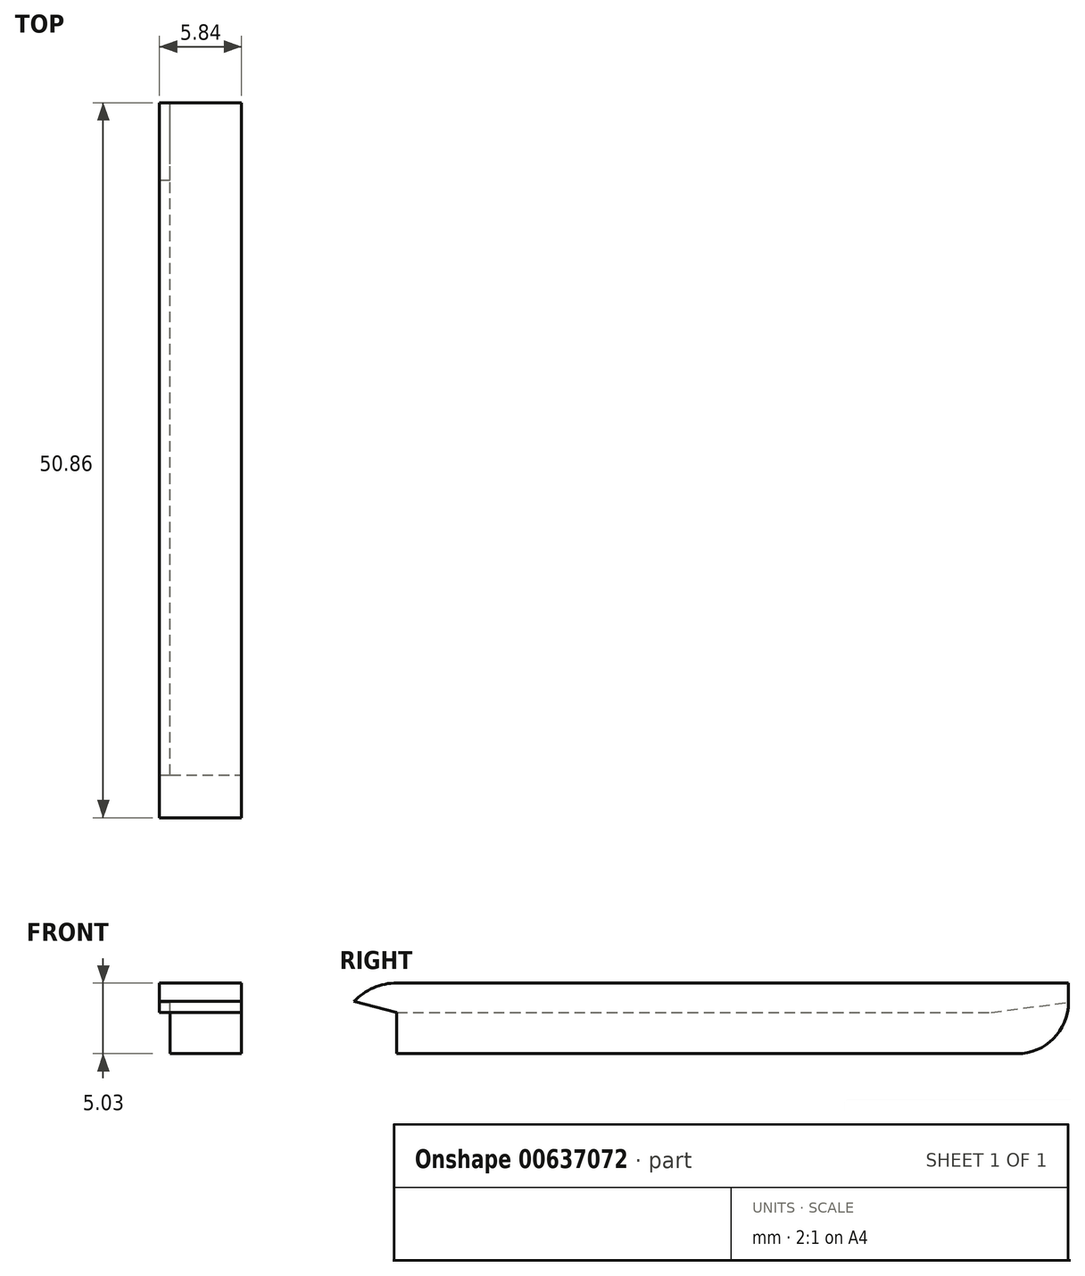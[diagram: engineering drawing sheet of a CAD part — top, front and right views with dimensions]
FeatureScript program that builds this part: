
annotation { "Feature Type Name" : "Feature", "Feature Type Description" : "" }
export const myFeature = defineFeature(function(context is Context, id is Id, definition is map)
    precondition{}
    {
        {
            var Q0;
            Q0=qCreatedBy(makeId("Right.planeOp"),FACE);
            var sketch = newSketch(context, id + "F0", { "sketchPlane" : qUnion([Q0])});
            skLineSegment(sketch, "E0", {"start": v(-27.86, 2.08) * mm, "end": v(14.45, 2.08) * mm});
            skArc(sketch, "E1", {"start": v(-27.86, 2.08) * mm, "mid": v(-29.52, 1.74) * mm, "end": v(-30.9, 0.77) * mm});
            skLineSegment(sketch, "E2", {"start": v(-30.9, 0.77) * mm, "end": v(-27.86, -0.01) * mm});
            skLineSegment(sketch, "E3", {"start": v(-27.86, 2.08) * mm, "end": v(-27.86, -2.95) * mm});
            skLineSegment(sketch, "E4", {"start": v(-27.86, -2.95) * mm, "end": v(14.45, -2.95) * mm});
            skArc(sketch, "E5", {"start": v(-27.86, -2.95) * mm, "mid": v(-30.18, -1.82) * mm, "end": v(-30.7, 0.71) * mm});
            skLineSegment(sketch, "E6", {"start": v(19.45, 2.08) * mm, "end": v(14.45, 2.08) * mm});
            skLineSegment(sketch, "E7", {"start": v(-27.86, -0.01) * mm, "end": v(14.45, -0.01) * mm});
            skLineSegment(sketch, "E8", {"start": v(14.45, -0.01) * mm, "end": v(14.45, 2.08) * mm});
            skLineSegment(sketch, "E9", {"start": v(14.45, -0.01) * mm, "end": v(14.45, -2.95) * mm});
            skArc(sketch, "E10", {"start": v(16.29, -2.95) * mm, "mid": v(18.88, -1.88) * mm, "end": v(19.95, 0.71) * mm});
            skLineSegment(sketch, "E11", {"start": v(16.29, -2.95) * mm, "end": v(14.45, -2.95) * mm});
            skLineSegment(sketch, "E12", {"start": v(14.45, -0.01) * mm, "end": v(19.95, 0.71) * mm});
            skLineSegment(sketch, "E13", {"start": v(19.95, 0.71) * mm, "end": v(19.95, 2.08) * mm});
            skLineSegment(sketch, "E14", {"start": v(19.95, 2.08) * mm, "end": v(19.45, 2.08) * mm});
            skSolve(sketch);
        }
        {
            var Q0;
            Q0=makeQuery(id+"F0.imprint","IMPRINT",FACE,{"disambiguationData":[TD([[makeQuery(id+"F0.imprint","IMPRINT",EDGE,{"derivedFrom":sQuery(id+"F0.wireOp",EDGE,"E6")}),1.0]])]});
            var Q1;
            {var subQ0=sQuery(id+"F0.wireOp",EDGE,"E0");Q1=makeQuery(id+"F0.imprint","IMPRINT",FACE,{"disambiguationData":[TD([[makeQuery(id+"F0.imprint","IMPRINT",EDGE,{"derivedFrom":subQ0}),-1.0]])]});}
            var Q2;
            {var subQ0=sQuery(id+"F0.wireOp",EDGE,"E1");Q2=makeQuery(id+"F0.imprint","IMPRINT",FACE,{"disambiguationData":[TD([[makeQuery(id+"F0.imprint","IMPRINT",EDGE,{"derivedFrom":subQ0}),1.0]])]});}
            extrude(context, id + "F1", {"entities" : qUnion([Q0, Q1, Q2]), "oppositeDirection" : true, "depth" : 5.84 * mm, "offsetDistance" : 25.4 * mm});
        }
        {
            var Q0;
            {var subQ3=sQuery(id+"F0.wireOp",EDGE,"E5");Q0=makeQuery(id+"F0.imprint","IMPRINT",FACE,{"disambiguationData":[TD([[makeQuery(id+"F0.imprint","IMPRINT",EDGE,{"derivedFrom":subQ3}),-1.0]])]});}
            var Q1;
            {var subQ2=sQuery(id+"F0.wireOp",EDGE,"E4");Q1=makeQuery(id+"F0.imprint","IMPRINT",FACE,{"disambiguationData":[TD([[makeQuery(id+"F0.imprint","IMPRINT",EDGE,{"derivedFrom":subQ2}),1.0]])]});}
            var Q2;
            Q2=makeQuery(id+"F0.imprint","IMPRINT",FACE,{"disambiguationData":[TD([[makeQuery(id+"F0.imprint","IMPRINT",EDGE,{"derivedFrom":sQuery(id+"F0.wireOp",EDGE,"E9")}),1.0]])]});
            extrude(context, id + "F2", {"entities" : qUnion([Q0, Q1, Q2]), "operationType" : NewBodyOperationType.ADD, "oppositeDirection" : true, "depth" : 5.08 * mm, "offsetDistance" : 25.4 * mm});
        }
    });
